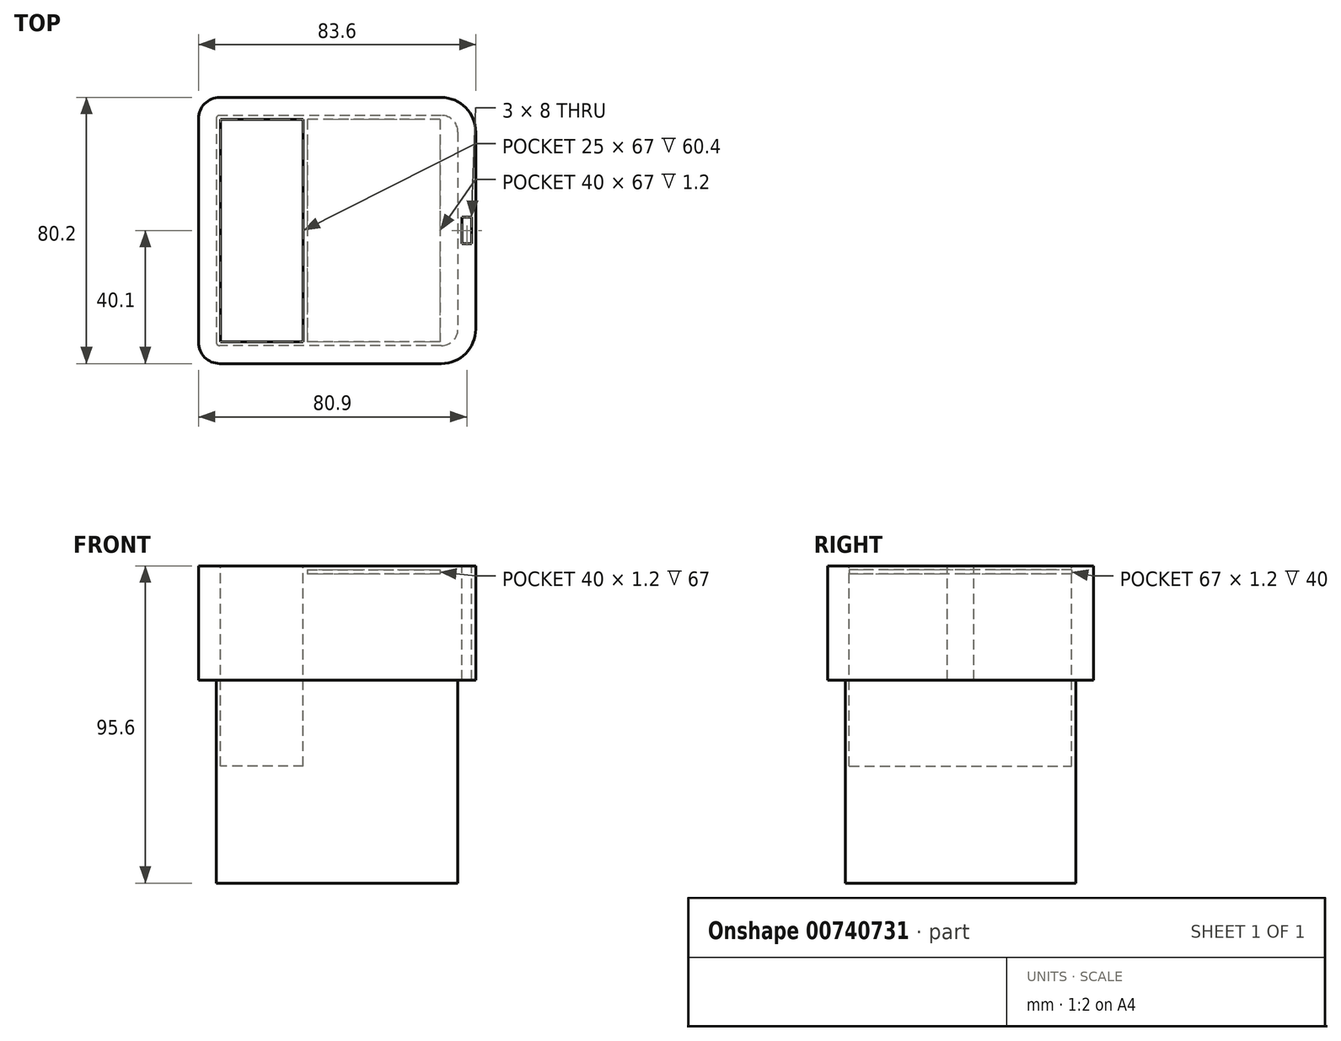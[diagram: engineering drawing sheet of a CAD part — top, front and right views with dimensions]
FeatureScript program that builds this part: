
annotation { "Feature Type Name" : "Feature", "Feature Type Description" : "" }
export const myFeature = defineFeature(function(context is Context, id is Id, definition is map)
    precondition{}
    {
        {
            var Q0;
            Q0=qCreatedBy(makeId("Top.planeOp"),FACE);
            var sketch = newSketch(context, id + "F0", { "sketchPlane" : qUnion([Q0])});
            skLineSegment(sketch, "E0.bottom", {"start": v(20, 33.5) * mm, "end": v(-20, 33.5) * mm});
            skLineSegment(sketch, "E0.top", {"start": v(20, -33.5) * mm, "end": v(-20, -33.5) * mm});
            skLineSegment(sketch, "E0.left", {"start": v(20, 33.5) * mm, "end": v(20, -33.5) * mm});
            skLineSegment(sketch, "E0.right", {"start": v(-20, 33.5) * mm, "end": v(-20, -33.5) * mm});
            skPoint(sketch, "E0.middle", {"position": v(0, 0) * mm});
            skLineSegment(sketch, "E1.0", {"start": v(-21.2, 34.7) * mm, "end": v(-21.2, -34.7) * mm});
            skLineSegment(sketch, "E1.1", {"start": v(21.2, 34.7) * mm, "end": v(-21.2, 34.7) * mm});
            skLineSegment(sketch, "E1.2", {"start": v(21.2, 34.7) * mm, "end": v(21.2, -34.7) * mm});
            skLineSegment(sketch, "E1.3", {"start": v(21.2, -34.7) * mm, "end": v(-21.2, -34.7) * mm});
            skSolve(sketch);
        }
        {
            var Q0;
            Q0=makeQuery(id+"F0.imprint","IMPRINT",FACE,{"disambiguationData":[TD([[makeQuery(id+"F0.imprint","IMPRINT",EDGE,{"derivedFrom":sQuery(id+"F0.wireOp",EDGE,"E0.bottom")}),1.0]])]});
            extrude(context, id + "F1", {"entities" : qUnion([Q0]), "depth" : 92 * mm, "offsetDistance" : 25.4 * mm});
        }
        {
            var Q0;
            Q0=makeQuery(id+"F0.imprint","IMPRINT",FACE,{"disambiguationData":[TD([[makeQuery(id+"F0.imprint","IMPRINT",EDGE,{"derivedFrom":sQuery(id+"F0.wireOp",EDGE,"E0.bottom")}),-1.0]])]});
            extrude(context, id + "F2", {"entities" : qUnion([Q0]), "depth" : 60 * mm, "offsetDistance" : 25.4 * mm});
        }
        {
            var Q0;
            Q0=makeQuery(id+"F0.imprint","IMPRINT",FACE,{"disambiguationData":[TD([[makeQuery(id+"F0.imprint","IMPRINT",EDGE,{"derivedFrom":sQuery(id+"F0.wireOp",EDGE,"E0.bottom")}),1.0]])]});
            var Q1;
            Q1=makeQuery(id+"F0.imprint","IMPRINT",FACE,{"disambiguationData":[TD([[makeQuery(id+"F0.imprint","IMPRINT",EDGE,{"derivedFrom":sQuery(id+"F0.wireOp",EDGE,"E0.bottom")}),-1.0]])]});
            extrude(context, id + "F3", {"entities" : qUnion([Q0, Q1]), "operationType" : NewBodyOperationType.ADD, "oppositeDirection" : true, "depth" : 1.2 * mm, "offsetDistance" : 25.4 * mm});
        }
        {
            var Q0;
            {var subQ0=sQuery(id+"F0.wireOp",EDGE,"E1.0");Q0=makeQuery(id+"F3.boolean.opBoolean","MERGE",FACE,{"derivedFrom":[makeQuery(id+"F2.opExtrude","SWEPT_FACE",FACE,{"disambiguationData":[OSD([subQ0])]}),makeQuery(id+"F3.opExtrude","SWEPT_FACE",FACE,{"disambiguationData":[OSD([subQ0])]})]});}
            extrude(context, id + "F4", {"entities" : qUnion([Q0]), "operationType" : NewBodyOperationType.ADD, "depth" : 25 * mm, "offsetDistance" : 25.4 * mm});
        }
        {
            var Q0;
            {var subQ0=sQuery(id+"F0.wireOp",EDGE,"E1.0");Q0=makeQuery(id+"F4.boolean.opBoolean","MERGE",FACE,{"derivedFrom":[makeQuery(id+"F2.opExtrude","CAP_FACE",FACE,{"disambiguationData":[OSD([sQuery(id+"F0.wireOp",EDGE,"E0.bottom"),sQuery(id+"F0.wireOp",EDGE,"E0.top"),sQuery(id+"F0.wireOp",EDGE,"E0.left"),sQuery(id+"F0.wireOp",EDGE,"E0.right"),subQ0,sQuery(id+"F0.wireOp",EDGE,"E1.1"),sQuery(id+"F0.wireOp",EDGE,"E1.2"),sQuery(id+"F0.wireOp",EDGE,"E1.3")])],"isStart":false}),makeQuery(id+"F4.opExtrude","SWEPT_FACE",FACE,{"disambiguationData":[OSD([subQ0]),TDD([makeQuery(id+"F2.opExtrude","CAP_EDGE",EDGE,{"disambiguationData":[OSD([subQ0])],"isStart":false})])]})]});}
            var sketch = newSketch(context, id + "F5", { "sketchPlane" : qUnion([Q0])});
            skLineSegment(sketch, "E2", {"start": v(-21.2, -34.7) * mm, "end": v(-21.2, 34.7) * mm});
            skLineSegment(sketch, "E3", {"start": v(-21.2, 0) * mm, "end": v(-46.2, 0) * mm, "construction": true});
            skLineSegment(sketch, "E4.bottom", {"start": v(-21.2, 33.5) * mm, "end": v(-46.2, 33.5) * mm});
            skLineSegment(sketch, "E4.top", {"start": v(-21.2, -33.5) * mm, "end": v(-46.2, -33.5) * mm});
            skLineSegment(sketch, "E4.left", {"start": v(-21.2, 33.5) * mm, "end": v(-21.2, -33.5) * mm, "construction": true});
            skLineSegment(sketch, "E4.right", {"start": v(-46.2, 33.5) * mm, "end": v(-46.2, -33.5) * mm});
            skPoint(sketch, "E4.middle", {"position": v(-33.7, 0) * mm});
            skSolve(sketch);
        }
        {
            var Q0;
            Q0=makeQuery(id+"F4.opExtrude","CAP_FACE",FACE,{"disambiguationData":[OSD([sQuery(id+"F0.wireOp",EDGE,"E1.0")])],"isStart":false});
            extrude(context, id + "F6", {"entities" : qUnion([Q0]), "operationType" : NewBodyOperationType.ADD, "depth" : 1.2 * mm, "offsetDistance" : 25.4 * mm});
        }
        {
            var Q0;
            {var subQ0=sQuery(id+"F5.wireOp",EDGE,"E4.bottom");Q0=makeQuery(id+"F5.imprint","IMPRINT",FACE,{"disambiguationData":[TD([[makeQuery(id+"F5.imprint","IMPRINT",EDGE,{"derivedFrom":subQ0}),1.0]])]});}
            extrude(context, id + "F7", {"entities" : qUnion([Q0]), "operationType" : NewBodyOperationType.REMOVE, "oppositeDirection" : true, "depth" : 26 * mm, "offsetDistance" : 25.4 * mm});
        }
        {
            var Q0;
            {var subQ0=sQuery(id+"F0.wireOp",EDGE,"E1.2");Q0=makeQuery(id+"F3.boolean.opBoolean","MERGE",FACE,{"derivedFrom":[makeQuery(id+"F2.opExtrude","SWEPT_FACE",FACE,{"disambiguationData":[OSD([subQ0])]}),makeQuery(id+"F3.opExtrude","SWEPT_FACE",FACE,{"disambiguationData":[OSD([subQ0])]})]});}
            extrude(context, id + "F8", {"entities" : qUnion([Q0]), "operationType" : NewBodyOperationType.ADD, "depth" : 4.2 * mm, "offsetDistance" : 25.4 * mm});
        }
        {
            var Q0;
            {var subQ0=sQuery(id+"F0.wireOp",EDGE,"E1.2");var subQ1=sQuery(id+"F0.wireOp",EDGE,"E1.0");var subQ2=makeQuery(id+"F2.opExtrude","CAP_EDGE",EDGE,{"disambiguationData":[OSD([subQ1])],"isStart":false});Q0=makeQuery(id+"F8.boolean.opBoolean","MERGE",FACE,{"derivedFrom":[makeQuery(id+"F6.boolean.opBoolean","MERGE",FACE,{"derivedFrom":[makeQuery(id+"F4.boolean.opBoolean","MERGE",FACE,{"derivedFrom":[makeQuery(id+"F2.opExtrude","CAP_FACE",FACE,{"disambiguationData":[OSD([sQuery(id+"F0.wireOp",EDGE,"E0.bottom"),sQuery(id+"F0.wireOp",EDGE,"E0.top"),sQuery(id+"F0.wireOp",EDGE,"E0.left"),sQuery(id+"F0.wireOp",EDGE,"E0.right"),subQ1,sQuery(id+"F0.wireOp",EDGE,"E1.1"),subQ0,sQuery(id+"F0.wireOp",EDGE,"E1.3")])],"isStart":false}),makeQuery(id+"F4.opExtrude","SWEPT_FACE",FACE,{"disambiguationData":[OSD([subQ1]),TDD([subQ2])]})]}),makeQuery(id+"F6.opExtrude","SWEPT_FACE",FACE,{"disambiguationData":[OSD([subQ1]),TDD([makeQuery(id+"F4.opExtrude","CAP_EDGE",EDGE,{"disambiguationData":[OSD([subQ1]),TDD([subQ2])],"isStart":false})])]})]}),makeQuery(id+"F8.opExtrude","SWEPT_FACE",FACE,{"disambiguationData":[OSD([subQ0]),TDD([makeQuery(id+"F2.opExtrude","CAP_EDGE",EDGE,{"disambiguationData":[OSD([subQ0])],"isStart":false})])]})]});}
            var sketch = newSketch(context, id + "F9", { "sketchPlane" : qUnion([Q0])});
            skLineSegment(sketch, "E5", {"start": v(21.2, -34.7) * mm, "end": v(21.2, 34.7) * mm});
            skLineSegment(sketch, "E6", {"start": v(24.2, 34.7) * mm, "end": v(24.2, -34.7) * mm});
            skSolve(sketch);
        }
        {
            var Q0;
            Q0=makeQuery(id+"F8.opExtrude","CAP_FACE",FACE,{"disambiguationData":[OSD([sQuery(id+"F0.wireOp",EDGE,"E1.2")])],"isStart":false});
            var sketch = newSketch(context, id + "F10", { "sketchPlane" : qUnion([Q0])});
            skPoint(sketch, "E7", {"position": v(0, 29.4) * mm});
            skPoint(sketch, "E7.positionSnap0", {"position": v(34.7, 29.4) * mm});
            skPoint(sketch, "E7.positionSnap1", {"position": v(0, 60) * mm});
            skCircle(sketch, "E8", {"center": v(0, 29.4) * mm, "radius": 4 * mm});
            skSolve(sketch);
        }
        {
            var Q0;
            {var subQ0=sQuery(id+"F0.wireOp",EDGE,"E1.1");var subQ1=sQuery(id+"F0.wireOp",EDGE,"E1.0");Q0=makeQuery(id+"F8.boolean.opBoolean","MERGE",FACE,{"derivedFrom":[makeQuery(id+"F6.boolean.opBoolean","MERGE",FACE,{"derivedFrom":[makeQuery(id+"F4.boolean.opBoolean","MERGE",FACE,{"derivedFrom":[makeQuery(id+"F3.boolean.opBoolean","MERGE",FACE,{"derivedFrom":[makeQuery(id+"F2.opExtrude","SWEPT_FACE",FACE,{"disambiguationData":[OSD([subQ0])]}),makeQuery(id+"F3.opExtrude","SWEPT_FACE",FACE,{"disambiguationData":[OSD([subQ0])]})]}),makeQuery(id+"F4.opExtrude","SWEPT_FACE",FACE,{"disambiguationData":[OSD([subQ1,subQ0])]})]}),makeQuery(id+"F6.opExtrude","SWEPT_FACE",FACE,{"disambiguationData":[OSD([subQ1,subQ0])]})]}),makeQuery(id+"F8.opExtrude","SWEPT_FACE",FACE,{"disambiguationData":[OSD([subQ0,sQuery(id+"F0.wireOp",EDGE,"E1.2")])]})]});}
            var sketch = newSketch(context, id + "F11", { "sketchPlane" : qUnion([Q0])});
            skPoint(sketch, "E9.0", {"position": v(-21.2, 60) * mm});
            skPoint(sketch, "E9.1", {"position": v(-24.2, 60) * mm});
            skLineSegment(sketch, "E10", {"start": v(-21.2, 60) * mm, "end": v(-21.2, -1.2) * mm});
            skLineSegment(sketch, "E11", {"start": v(-24.2, 60) * mm, "end": v(-24.2, -1.2) * mm});
            skLineSegment(sketch, "E12", {"start": v(-24.2, 29.4) * mm, "end": v(-21.2, 29.4) * mm, "construction": true});
            skLineSegment(sketch, "E13", {"start": v(-24.2, 33.65) * mm, "end": v(-21.2, 33.65) * mm});
            skLineSegment(sketch, "E14", {"start": v(-21.2, 25.4) * mm, "end": v(-24.2, 25.4) * mm});
            skSolve(sketch);
        }
        {
            var Q0;
            {var subQ0=sQuery(id+"F11.wireOp",EDGE,"E13");Q0=makeQuery(id+"F11.imprint","IMPRINT",FACE,{"disambiguationData":[TD([[makeQuery(id+"F11.imprint","IMPRINT",EDGE,{"derivedFrom":subQ0}),-1.0]])]});}
            extrude(context, id + "F12", {"entities" : qUnion([Q0]), "operationType" : NewBodyOperationType.REMOVE, "oppositeDirection" : true, "depth" : 38.7 * mm, "offsetDistance" : 25 * mm});
        }
        {
            var Q0;
            Q0=makeQuery(id+"F8.opExtrude","CAP_EDGE",EDGE,{"disambiguationData":[OSD([sQuery(id+"F0.wireOp",EDGE,"E1.2"),sQuery(id+"F0.wireOp",EDGE,"E1.3")])],"isStart":false});
            var Q1;
            Q1=makeQuery(id+"F8.opExtrude","CAP_EDGE",EDGE,{"disambiguationData":[OSD([sQuery(id+"F0.wireOp",EDGE,"E1.1"),sQuery(id+"F0.wireOp",EDGE,"E1.2")])],"isStart":false});
            fillet(context, id + "F13", {"entities" : qUnion([Q0, Q1]), "radius" : 5 * mm, "tangentPropagation" : true, "allowEdgeOverflow" : false});
        }
        {
            var Q0;
            Q0=makeQuery(id+"F6.opExtrude","CAP_EDGE",EDGE,{"disambiguationData":[OSD([sQuery(id+"F0.wireOp",EDGE,"E1.0"),sQuery(id+"F0.wireOp",EDGE,"E1.1")])],"isStart":false});
            var Q1;
            Q1=makeQuery(id+"F6.opExtrude","CAP_EDGE",EDGE,{"disambiguationData":[OSD([sQuery(id+"F0.wireOp",EDGE,"E1.0"),sQuery(id+"F0.wireOp",EDGE,"E1.3")])],"isStart":false});
            fillet(context, id + "F14", {"entities" : qUnion([Q0, Q1]), "radius" : 1 * mm, "tangentPropagation" : true, "allowEdgeOverflow" : false});
        }
        {
            var Q0;
            {var subQ2=sQuery(id+"F9.wireOp",EDGE,"E5");Q0=makeQuery(id+"F9.imprint","IMPRINT",FACE,{"disambiguationData":[TD([[makeQuery(id+"F9.imprint","IMPRINT",EDGE,{"derivedFrom":subQ2}),1.0]])]});}
            var sketch = newSketch(context, id + "F15", { "sketchPlane" : qUnion([Q0])});
            skLineSegment(sketch, "E15.0", {"start": v(25.4, 29.7) * mm, "end": v(25.4, -29.7) * mm});
            skArc(sketch, "E15.1", {"start": v(25.4, 29.7) * mm, "mid": v(23.94, 33.24) * mm, "end": v(20.4, 34.7) * mm});
            skLineSegment(sketch, "E15.2", {"start": v(20.4, 34.7) * mm, "end": v(-46.4, 34.7) * mm});
            skArc(sketch, "E15.3", {"start": v(20.4, -34.7) * mm, "mid": v(23.94, -33.24) * mm, "end": v(25.4, -29.7) * mm});
            skLineSegment(sketch, "E15.4", {"start": v(20.4, -34.7) * mm, "end": v(-46.4, -34.7) * mm});
            skArc(sketch, "E15.5", {"start": v(-46.4, 34.7) * mm, "mid": v(-47.1, 34.4) * mm, "end": v(-47.4, 33.7) * mm});
            skLineSegment(sketch, "E15.6", {"start": v(-47.4, 33.7) * mm, "end": v(-47.4, -33.7) * mm});
            skArc(sketch, "E15.7", {"start": v(-47.4, -33.7) * mm, "mid": v(-47.1, -34.4) * mm, "end": v(-46.4, -34.7) * mm});
            skLineSegment(sketch, "E16.0", {"start": v(20, -33.5) * mm, "end": v(-20, -33.5) * mm});
            skLineSegment(sketch, "E16.1", {"start": v(20, 33.5) * mm, "end": v(20, -33.5) * mm});
            skLineSegment(sketch, "E16.2", {"start": v(-20, 33.5) * mm, "end": v(-20, -33.5) * mm});
            skLineSegment(sketch, "E16.3", {"start": v(20, 33.5) * mm, "end": v(-20, 33.5) * mm});
            skArc(sketch, "E17.0", {"start": v(30.8, 29.7) * mm, "mid": v(27.75, 37.05) * mm, "end": v(20.4, 40.1) * mm});
            skLineSegment(sketch, "E17.1", {"start": v(20.4, 40.1) * mm, "end": v(-46.4, 40.1) * mm});
            skLineSegment(sketch, "E17.2", {"start": v(30.8, 29.7) * mm, "end": v(30.8, -29.7) * mm});
            skArc(sketch, "E17.3", {"start": v(-46.4, 40.1) * mm, "mid": v(-50.93, 38.23) * mm, "end": v(-52.8, 33.7) * mm});
            skArc(sketch, "E17.4", {"start": v(20.4, -40.1) * mm, "mid": v(27.75, -37.05) * mm, "end": v(30.8, -29.7) * mm});
            skLineSegment(sketch, "E17.5", {"start": v(20.4, -40.1) * mm, "end": v(-46.4, -40.1) * mm});
            skArc(sketch, "E17.6", {"start": v(-52.8, -33.7) * mm, "mid": v(-50.93, -38.23) * mm, "end": v(-46.4, -40.1) * mm});
            skLineSegment(sketch, "E17.7", {"start": v(-52.8, 33.7) * mm, "end": v(-52.8, -33.7) * mm});
            skSolve(sketch);
        }
        {
            var Q0;
            Q0 = qSketchRegion(id + "F15", true);
            var Q1;
            {var subQ0=sQuery(id+"F15.wireOp",EDGE,"E15.2");Q1=makeQuery(id+"F15.imprint","IMPRINT",FACE,{"disambiguationData":[TD([[makeQuery(id+"F15.imprint","IMPRINT",EDGE,{"derivedFrom":subQ0}),1.0]])]});}
            var Q2;
            {var subQ0=sQuery(id+"F15.wireOp",EDGE,"E15.0");Q2=makeQuery(id+"F15.imprint","IMPRINT",FACE,{"disambiguationData":[TD([[makeQuery(id+"F15.imprint","IMPRINT",EDGE,{"derivedFrom":subQ0}),-1.0]])]});}
            var Q3;
            Q3=makeQuery(id+"F15.imprint","IMPRINT",FACE,{"disambiguationData":[TD([[makeQuery(id+"F15.imprint","IMPRINT",EDGE,{"derivedFrom":makeQuery(id+"F9.imprint","IMPRINT",EDGE,{"derivedFrom":makeQuery(id+"F7.boolean.opBoolean","COPY",EDGE,{"derivedFrom":makeQuery(id+"F7.opExtrude","CAP_EDGE",EDGE,{"disambiguationData":[OSD([sQuery(id+"F5.wireOp",EDGE,"E2")])],"isStart":true})})})}),1.0]])]});
            extrude(context, id + "F16", {"entities" : qUnion([Q0, Q1, Q2, Q3]), "depth" : 34.4 * mm, "offsetDistance" : 25 * mm});
        }
        {
            var Q0;
            Q0=makeQuery(id+"F16.opExtrude","SWEPT_FACE",FACE,{"disambiguationData":[OSD([sQuery(id+"F15.wireOp",EDGE,"E16.0")])]});
            var sketch = newSketch(context, id + "F17", { "sketchPlane" : qUnion([Q0])});
            skLineSegment(sketch, "E18", {"start": v(20, 93.2) * mm, "end": v(-20, 93.2) * mm});
            skSolve(sketch);
        }
        {
            var Q0;
            {var subQ0=sQuery(id+"F17.wireOp",EDGE,"E18");Q0=makeQuery(id+"F17.imprint","IMPRINT",FACE,{"disambiguationData":[TD([[makeQuery(id+"F17.imprint","IMPRINT",EDGE,{"derivedFrom":subQ0}),-1.0]])]});}
            extrude(context, id + "F18", {"entities" : qUnion([Q0]), "operationType" : NewBodyOperationType.ADD, "endBound" : BoundingType.UP_TO_NEXT, "depth" : 25 * mm, "offsetDistance" : 25 * mm});
        }
        {
            var Q0;
            Q0=makeQuery(id+"F16.opExtrude","CAP_FACE",FACE,{"disambiguationData":[OSD([sQuery(id+"F15.wireOp",EDGE,"E16.0"),sQuery(id+"F15.wireOp",EDGE,"E16.1"),sQuery(id+"F15.wireOp",EDGE,"E16.2"),sQuery(id+"F15.wireOp",EDGE,"E16.3"),sQuery(id+"F15.wireOp",EDGE,"E17.0"),sQuery(id+"F15.wireOp",EDGE,"E17.1"),sQuery(id+"F15.wireOp",EDGE,"E17.2"),sQuery(id+"F15.wireOp",EDGE,"E17.3"),sQuery(id+"F15.wireOp",EDGE,"E17.4"),sQuery(id+"F15.wireOp",EDGE,"E17.5"),sQuery(id+"F15.wireOp",EDGE,"E17.6"),sQuery(id+"F15.wireOp",EDGE,"E17.7")])],"isStart":true});
            var sketch = newSketch(context, id + "F19", { "sketchPlane" : qUnion([Q0])});
            skArc(sketch, "E19.0", {"start": v(25.4, -29.7) * mm, "mid": v(23.94, -33.24) * mm, "end": v(20.4, -34.7) * mm});
            skLineSegment(sketch, "E19.1", {"start": v(20.4, -34.7) * mm, "end": v(-46.4, -34.7) * mm});
            skLineSegment(sketch, "E19.2", {"start": v(25.4, -29.7) * mm, "end": v(25.4, 29.7) * mm});
            skArc(sketch, "E19.3", {"start": v(20.4, 40.1) * mm, "mid": v(27.75, 37.05) * mm, "end": v(30.8, 29.7) * mm});
            skLineSegment(sketch, "E19.4", {"start": v(30.8, -29.7) * mm, "end": v(30.8, 29.7) * mm});
            skArc(sketch, "E19.5", {"start": v(20.4, 34.7) * mm, "mid": v(23.94, 33.24) * mm, "end": v(25.4, 29.7) * mm});
            skLineSegment(sketch, "E19.6", {"start": v(20.4, 40.1) * mm, "end": v(-46.4, 40.1) * mm});
            skLineSegment(sketch, "E19.7", {"start": v(20.4, 34.7) * mm, "end": v(-46.4, 34.7) * mm});
            skLineSegment(sketch, "E19.8", {"start": v(-52.8, -33.7) * mm, "end": v(-52.8, 33.7) * mm});
            skLineSegment(sketch, "E19.9", {"start": v(-47.4, -33.7) * mm, "end": v(-47.4, 33.7) * mm});
            skArc(sketch, "E19.10", {"start": v(-47.4, 33.7) * mm, "mid": v(-47.1, 34.4) * mm, "end": v(-46.4, 34.7) * mm});
            skArc(sketch, "E19.11", {"start": v(-52.8, 33.7) * mm, "mid": v(-50.93, 38.23) * mm, "end": v(-46.4, 40.1) * mm});
            skArc(sketch, "E19.12", {"start": v(-46.4, -40.1) * mm, "mid": v(-50.93, -38.23) * mm, "end": v(-52.8, -33.7) * mm});
            skArc(sketch, "E19.13", {"start": v(-46.4, -34.7) * mm, "mid": v(-47.1, -34.4) * mm, "end": v(-47.4, -33.7) * mm});
            skLineSegment(sketch, "E19.14", {"start": v(20.4, -40.1) * mm, "end": v(-46.4, -40.1) * mm});
            skSolve(sketch);
        }
        {
            var Q0;
            Q0=makeQuery(id+"F19.imprint","IMPRINT",FACE,{"disambiguationData":[TD([[makeQuery(id+"F19.imprint","IMPRINT",EDGE,{"derivedFrom":sQuery(id+"F19.wireOp",EDGE,"E19.0")}),1.0]])]});
            var Q1;
            {var subQ0=sQuery(id+"F0.wireOp",EDGE,"E1.2");var subQ1=sQuery(id+"F0.wireOp",EDGE,"E1.0");var subQ2=makeQuery(id+"F3.opExtrude","CAP_EDGE",EDGE,{"disambiguationData":[OSD([subQ1])],"isStart":false});Q1=makeQuery(id+"F8.boolean.opBoolean","MERGE",FACE,{"derivedFrom":[makeQuery(id+"F6.boolean.opBoolean","MERGE",FACE,{"derivedFrom":[makeQuery(id+"F4.boolean.opBoolean","MERGE",FACE,{"derivedFrom":[makeQuery(id+"F3.opExtrude","CAP_FACE",FACE,{"disambiguationData":[OSD([subQ1,sQuery(id+"F0.wireOp",EDGE,"E1.1"),subQ0,sQuery(id+"F0.wireOp",EDGE,"E1.3")])],"isStart":false}),makeQuery(id+"F4.opExtrude","SWEPT_FACE",FACE,{"disambiguationData":[OSD([subQ1]),TDD([subQ2])]})]}),makeQuery(id+"F6.opExtrude","SWEPT_FACE",FACE,{"disambiguationData":[OSD([subQ1]),TDD([makeQuery(id+"F4.opExtrude","CAP_EDGE",EDGE,{"disambiguationData":[OSD([subQ1]),TDD([subQ2])],"isStart":false})])]})]}),makeQuery(id+"F8.opExtrude","SWEPT_FACE",FACE,{"disambiguationData":[OSD([subQ0]),TDD([makeQuery(id+"F3.opExtrude","CAP_EDGE",EDGE,{"disambiguationData":[OSD([subQ0])],"isStart":false})])]})]});}
            extrude(context, id + "F20", {"entities" : qUnion([Q0]), "operationType" : NewBodyOperationType.ADD, "endBound" : BoundingType.UP_TO_SURFACE, "depth" : 25 * mm, "endBoundEntityFace" : qUnion([Q1]), "offsetDistance" : 25 * mm});
        }
        {
            var Q0;
            {var subQ0=sQuery(id+"F15.wireOp",EDGE,"E16.0");Q0=makeQuery(id+"F18.boolean.opBoolean","MERGE",FACE,{"derivedFrom":[makeQuery(id+"F16.opExtrude","CAP_FACE",FACE,{"disambiguationData":[OSD([subQ0,sQuery(id+"F15.wireOp",EDGE,"E16.1"),sQuery(id+"F15.wireOp",EDGE,"E16.2"),sQuery(id+"F15.wireOp",EDGE,"E16.3"),sQuery(id+"F15.wireOp",EDGE,"E17.0"),sQuery(id+"F15.wireOp",EDGE,"E17.1"),sQuery(id+"F15.wireOp",EDGE,"E17.2"),sQuery(id+"F15.wireOp",EDGE,"E17.3"),sQuery(id+"F15.wireOp",EDGE,"E17.4"),sQuery(id+"F15.wireOp",EDGE,"E17.5"),sQuery(id+"F15.wireOp",EDGE,"E17.6"),sQuery(id+"F15.wireOp",EDGE,"E17.7")])],"isStart":false}),makeQuery(id+"F18.opExtrude","SWEPT_FACE",FACE,{"disambiguationData":[OSD([subQ0])]})]});}
            var sketch = newSketch(context, id + "F21", { "sketchPlane" : qUnion([Q0])});
            skLineSegment(sketch, "E20", {"start": v(30.8, 0) * mm, "end": v(28.1, 0) * mm});
            skLineSegment(sketch, "E21.bottom", {"start": v(29.6, -4) * mm, "end": v(26.6, -4) * mm});
            skLineSegment(sketch, "E21.top", {"start": v(29.6, 4) * mm, "end": v(26.6, 4) * mm});
            skLineSegment(sketch, "E21.left", {"start": v(29.6, -4) * mm, "end": v(29.6, 4) * mm});
            skLineSegment(sketch, "E21.right", {"start": v(26.6, -4) * mm, "end": v(26.6, 4) * mm});
            skPoint(sketch, "E21.middle", {"position": v(28.1, 0) * mm});
            skPoint(sketch, "E22.0", {"position": v(25.4, 0) * mm});
            skSolve(sketch);
        }
        {
            var Q0;
            {var subQ3=sQuery(id+"F21.wireOp",EDGE,"E21.bottom");Q0=makeQuery(id+"F21.imprint","IMPRINT",FACE,{"disambiguationData":[TD([[makeQuery(id+"F21.imprint","IMPRINT",EDGE,{"derivedFrom":subQ3}),-1.0]])]});}
            extrude(context, id + "F22", {"entities" : qUnion([Q0]), "operationType" : NewBodyOperationType.REMOVE, "oppositeDirection" : true, "depth" : 69 * mm, "offsetDistance" : 25 * mm});
        }
    });
